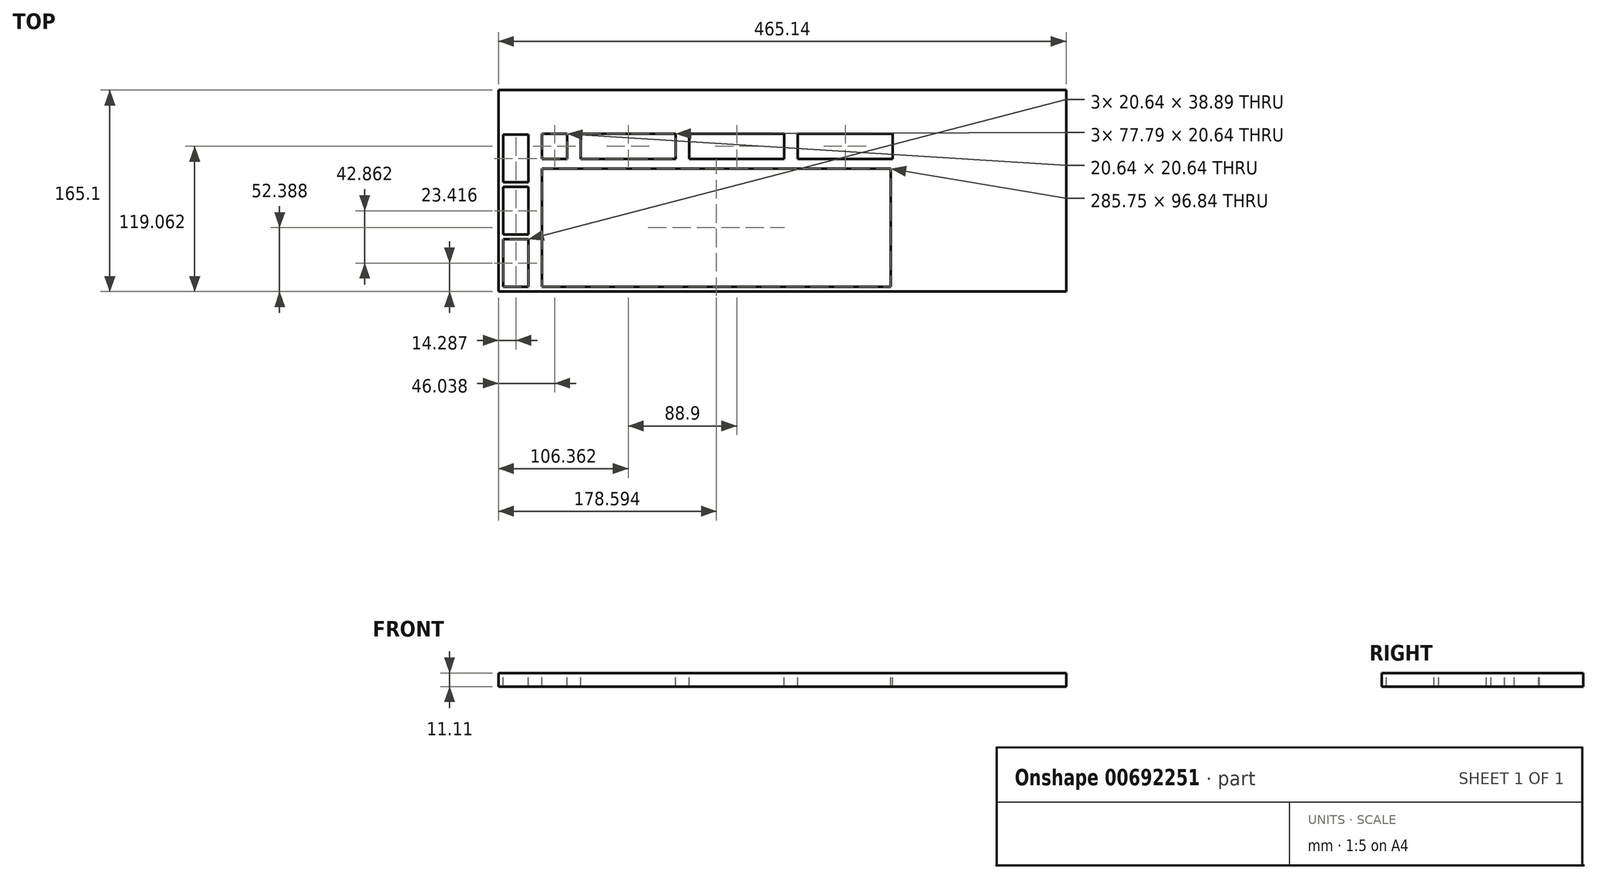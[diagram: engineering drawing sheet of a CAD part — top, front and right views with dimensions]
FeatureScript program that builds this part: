
annotation { "Feature Type Name" : "Feature", "Feature Type Description" : "" }
export const myFeature = defineFeature(function(context is Context, id is Id, definition is map)
    precondition{}
    {
        {
            var Q0;
            Q0=qCreatedBy(makeId("Top.planeOp"),FACE);
            var sketch = newSketch(context, id + "F0", { "sketchPlane" : qUnion([Q0])});
            skLineSegment(sketch, "E0.bottom", {"start": v(0, 0) * mm, "end": v(465.14, 0) * mm});
            skLineSegment(sketch, "E0.top", {"start": v(0, 165.1) * mm, "end": v(465.14, 165.1) * mm});
            skLineSegment(sketch, "E0.left", {"start": v(0, 0) * mm, "end": v(0, 165.1) * mm});
            skLineSegment(sketch, "E0.right", {"start": v(465.14, 0) * mm, "end": v(465.14, 165.1) * mm});
            skSolve(sketch);
        }
        {
            var Q0;
            Q0=makeQuery(id+"F0.imprint","IMPRINT",FACE,{"disambiguationData":[TD([[makeQuery(id+"F0.imprint","IMPRINT",EDGE,{"derivedFrom":sQuery(id+"F0.wireOp",EDGE,"E0.bottom")}),1.0]])]});
            extrude(context, id + "F1", {"entities" : qUnion([Q0]), "depth" : 11.1 * mm, "offsetDistance" : 25.4 * mm});
        }
        {
            var Q0;
            Q0=makeQuery(id+"F1.opExtrude","CAP_FACE",FACE,{"disambiguationData":[OSD([sQuery(id+"F0.wireOp",EDGE,"E0.bottom"),sQuery(id+"F0.wireOp",EDGE,"E0.top"),sQuery(id+"F0.wireOp",EDGE,"E0.left"),sQuery(id+"F0.wireOp",EDGE,"E0.right")])],"isStart":false});
            var sketch = newSketch(context, id + "F2", { "sketchPlane" : qUnion([Q0])});
            skLineSegment(sketch, "E1.bottom", {"start": v(3.97, 3.97) * mm, "end": v(24.6, 3.97) * mm});
            skLineSegment(sketch, "E1.top", {"start": v(3.97, 42.86) * mm, "end": v(24.6, 42.86) * mm});
            skLineSegment(sketch, "E1.left", {"start": v(3.97, 3.97) * mm, "end": v(3.97, 42.86) * mm});
            skLineSegment(sketch, "E1.right", {"start": v(24.6, 3.97) * mm, "end": v(24.6, 42.86) * mm});
            skLineSegment(sketch, "E2.bottom", {"start": v(3.97, 46.83) * mm, "end": v(24.6, 46.83) * mm});
            skLineSegment(sketch, "E2.top", {"start": v(3.97, 85.72) * mm, "end": v(24.6, 85.72) * mm});
            skLineSegment(sketch, "E2.left", {"start": v(3.97, 46.83) * mm, "end": v(3.97, 85.72) * mm});
            skLineSegment(sketch, "E2.right", {"start": v(24.6, 46.83) * mm, "end": v(24.6, 85.72) * mm});
            skLineSegment(sketch, "E3.bottom", {"start": v(3.97, 89.7) * mm, "end": v(24.6, 89.7) * mm});
            skLineSegment(sketch, "E3.top", {"start": v(3.97, 128.59) * mm, "end": v(24.6, 128.59) * mm});
            skLineSegment(sketch, "E3.left", {"start": v(3.97, 89.7) * mm, "end": v(3.97, 128.59) * mm});
            skLineSegment(sketch, "E3.right", {"start": v(24.6, 89.7) * mm, "end": v(24.6, 128.59) * mm});
            skLineSegment(sketch, "E4.bottom", {"start": v(35.72, 3.97) * mm, "end": v(321.47, 3.97) * mm});
            skLineSegment(sketch, "E4.top", {"start": v(35.72, 100.8) * mm, "end": v(321.47, 100.8) * mm});
            skLineSegment(sketch, "E4.left", {"start": v(35.72, 3.97) * mm, "end": v(35.72, 100.8) * mm});
            skLineSegment(sketch, "E4.right", {"start": v(321.47, 3.97) * mm, "end": v(321.47, 100.8) * mm});
            skLineSegment(sketch, "E5.bottom", {"start": v(67.47, 129.38) * mm, "end": v(145.26, 129.38) * mm});
            skLineSegment(sketch, "E5.top", {"start": v(67.47, 108.74) * mm, "end": v(145.26, 108.74) * mm});
            skLineSegment(sketch, "E5.left", {"start": v(67.47, 129.38) * mm, "end": v(67.47, 108.74) * mm});
            skLineSegment(sketch, "E5.right", {"start": v(145.26, 129.38) * mm, "end": v(145.26, 108.74) * mm});
            skLineSegment(sketch, "E6.bottom", {"start": v(156.37, 129.38) * mm, "end": v(234.16, 129.38) * mm});
            skLineSegment(sketch, "E6.top", {"start": v(156.37, 108.74) * mm, "end": v(234.16, 108.74) * mm});
            skLineSegment(sketch, "E6.left", {"start": v(156.37, 129.38) * mm, "end": v(156.37, 108.74) * mm});
            skLineSegment(sketch, "E6.right", {"start": v(234.16, 129.38) * mm, "end": v(234.16, 108.74) * mm});
            skLineSegment(sketch, "E7.bottom", {"start": v(245.27, 129.38) * mm, "end": v(323.06, 129.38) * mm});
            skLineSegment(sketch, "E7.top", {"start": v(245.27, 108.74) * mm, "end": v(323.06, 108.74) * mm});
            skLineSegment(sketch, "E7.left", {"start": v(245.27, 129.38) * mm, "end": v(245.27, 108.74) * mm});
            skLineSegment(sketch, "E7.right", {"start": v(323.06, 129.38) * mm, "end": v(323.06, 108.74) * mm});
            skLineSegment(sketch, "E8.bottom", {"start": v(35.72, 129.38) * mm, "end": v(56.36, 129.38) * mm});
            skLineSegment(sketch, "E8.top", {"start": v(35.72, 108.74) * mm, "end": v(56.36, 108.74) * mm});
            skLineSegment(sketch, "E8.left", {"start": v(35.72, 129.38) * mm, "end": v(35.72, 108.74) * mm});
            skLineSegment(sketch, "E8.right", {"start": v(56.36, 129.38) * mm, "end": v(56.36, 108.74) * mm});
            skSolve(sketch);
        }
        {
            var Q0;
            Q0 = qSketchRegion(id + "F2", true);
            extrude(context, id + "F3", {"entities" : qUnion([Q0]), "operationType" : NewBodyOperationType.REMOVE, "endBound" : BoundingType.THROUGH_ALL, "oppositeDirection" : true, "depth" : 25.4 * mm, "offsetDistance" : 25.4 * mm});
        }
    });
